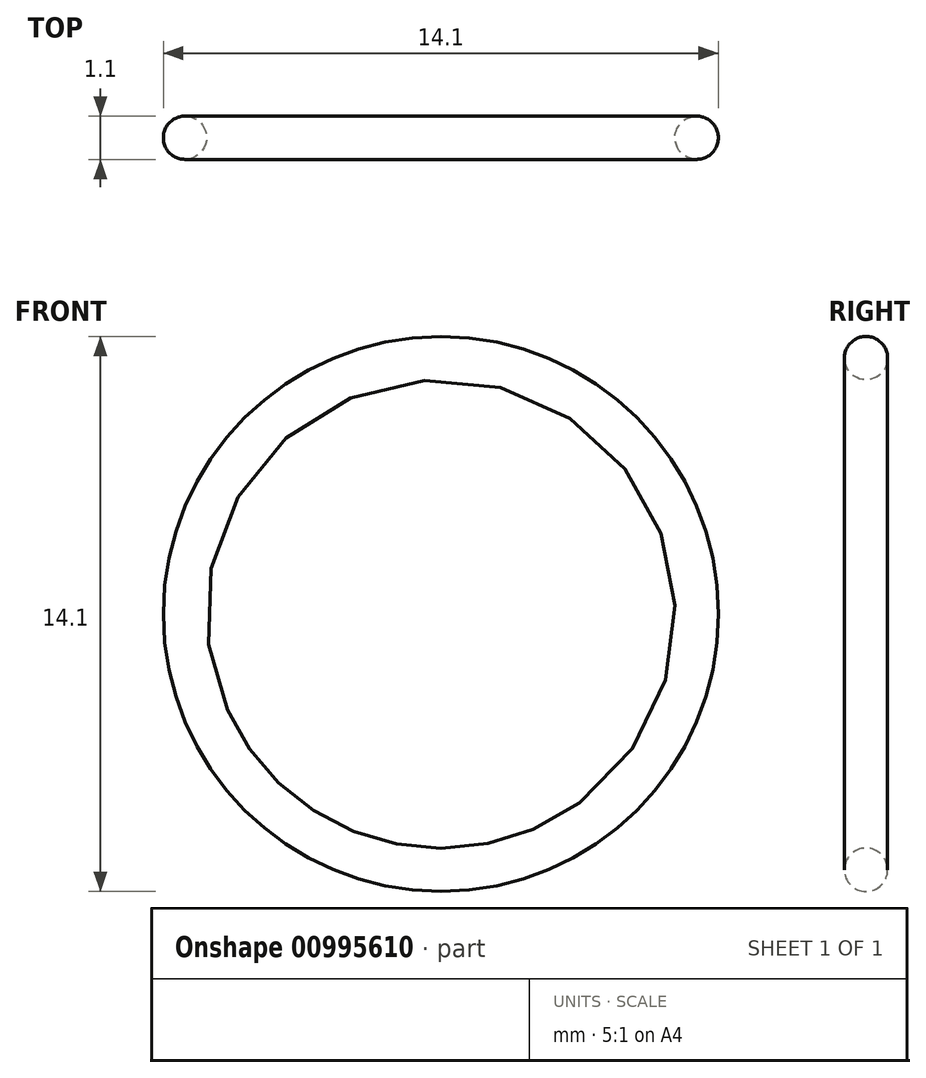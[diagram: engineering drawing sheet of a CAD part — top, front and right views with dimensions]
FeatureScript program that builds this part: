
annotation { "Feature Type Name" : "Feature", "Feature Type Description" : "" }
export const myFeature = defineFeature(function(context is Context, id is Id, definition is map)
    precondition{}
    {
        {
            var Q0;
            Q0=qCreatedBy(makeId("Right.planeOp"),FACE);
            var sketch = newSketch(context, id + "F0", { "sketchPlane" : qUnion([Q0])});
            skCircle(sketch, "E0", {"center": v(0, 6.5) * mm, "radius": 0.55 * mm});
            skLineSegment(sketch, "E1", {"start": v(-3.27, 0) * mm, "end": v(6.34, 0) * mm, "construction": true});
            skSolve(sketch);
        }
        {
            var Q0;
            Q0 = qSketchRegion(id + "F0", true);
            var Q1;
            Q1=sQuery(id+"F0.wireOp",EDGE,"E1");
            revolve(context, id + "F1", {"surfaceOperationType" : NewSurfaceOperationType.NEW, "entities" : qUnion([Q0]), "axis" : qUnion([Q1]), "revolveType" : RevolveType.FULL});
        }
    });
